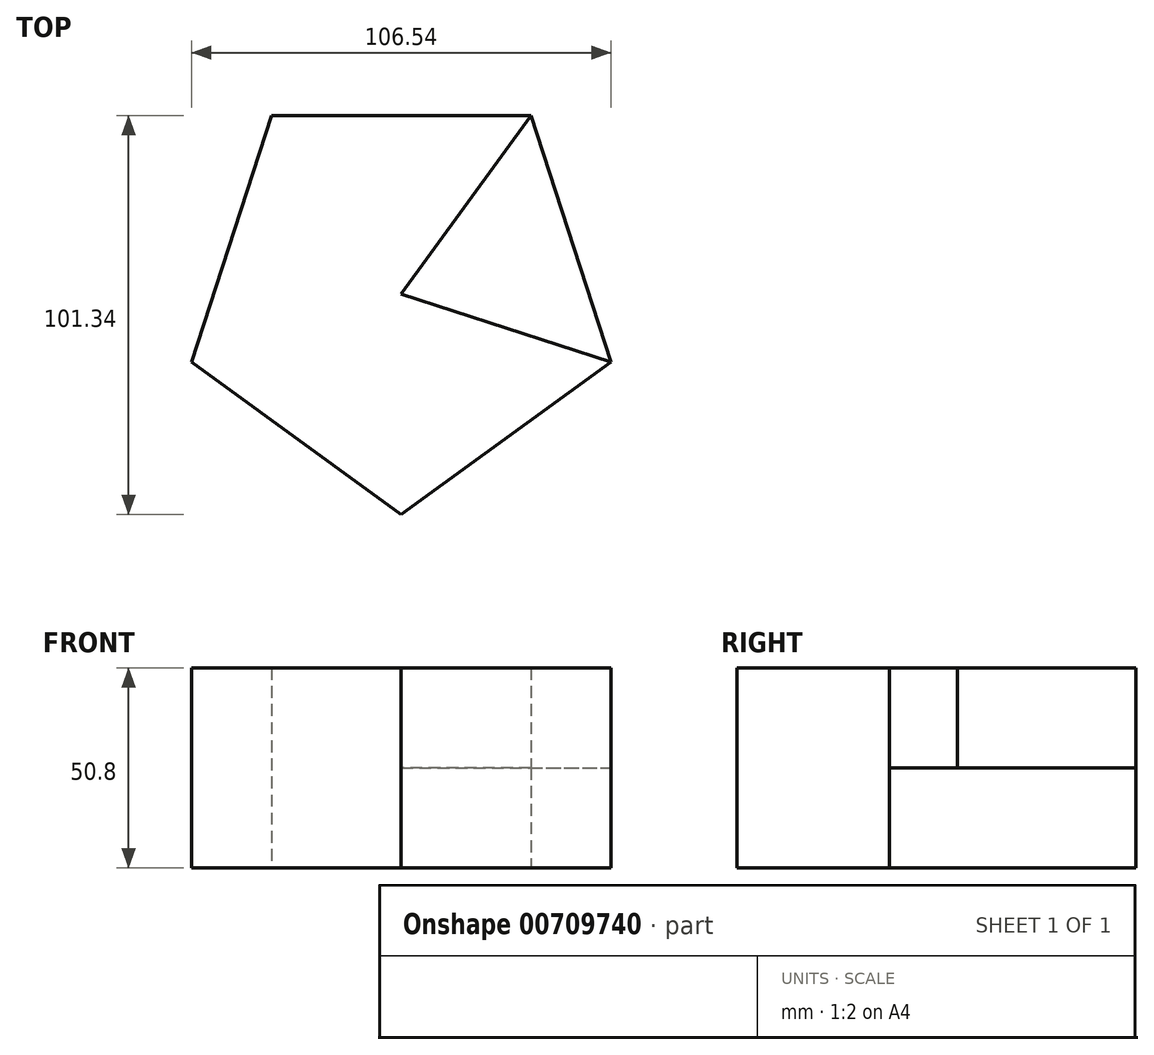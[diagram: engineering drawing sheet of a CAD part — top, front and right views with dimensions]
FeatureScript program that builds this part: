
annotation { "Feature Type Name" : "Feature", "Feature Type Description" : "" }
export const myFeature = defineFeature(function(context is Context, id is Id, definition is map)
    precondition{}
    {
        {
            var Q0;
            Q0=qCreatedBy(makeId("Top.planeOp"),FACE);
            var sketch = newSketch(context, id + "F0", { "sketchPlane" : qUnion([Q0])});
            skCircle(sketch, "E0.cCircle", {"center": v(0, 0) * mm, "radius": 45.32 * mm, "construction": true});
            skLineSegment(sketch, "E0.0", {"start": v(-32.93, 45.32) * mm, "end": v(32.93, 45.32) * mm});
            skLineSegment(sketch, "E0.1", {"start": v(32.93, 45.32) * mm, "end": v(53.27, -17.3) * mm});
            skLineSegment(sketch, "E0.2", {"start": v(53.27, -17.3) * mm, "end": v(0, -56.02) * mm});
            skLineSegment(sketch, "E0.3", {"start": v(0, -56.02) * mm, "end": v(-53.27, -17.3) * mm});
            skLineSegment(sketch, "E0.4", {"start": v(-53.27, -17.3) * mm, "end": v(-32.93, 45.32) * mm});
            skPoint(sketch, "E0.0.midPoint", {"position": v(0, 45.32) * mm});
            skSolve(sketch);
        }
        {
            var Q0;
            Q0=makeQuery(id+"F0.imprint","IMPRINT",FACE,{"disambiguationData":[TD([[makeQuery(id+"F0.imprint","IMPRINT",EDGE,{"derivedFrom":sQuery(id+"F0.wireOp",EDGE,"E0.0")}),-1.0]])]});
            extrude(context, id + "F1", {"entities" : qUnion([Q0]), "depth" : 25.4 * mm, "offsetDistance" : 25.4 * mm});
        }
        {
            var Q0;
            Q0=makeQuery(id+"F1.opExtrude","CAP_FACE",FACE,{"disambiguationData":[OSD([sQuery(id+"F0.wireOp",EDGE,"E0.0"),sQuery(id+"F0.wireOp",EDGE,"E0.1"),sQuery(id+"F0.wireOp",EDGE,"E0.2"),sQuery(id+"F0.wireOp",EDGE,"E0.3"),sQuery(id+"F0.wireOp",EDGE,"E0.4")])],"isStart":false});
            var sketch = newSketch(context, id + "F2", { "sketchPlane" : qUnion([Q0])});
            skLineSegment(sketch, "E1", {"start": v(32.93, 45.32) * mm, "end": v(0, 0) * mm});
            skLineSegment(sketch, "E2", {"start": v(0, 0) * mm, "end": v(53.27, -17.3) * mm});
            skSolve(sketch);
        }
        {
            var Q0;
            Q0=makeQuery(id+"F2.imprint","IMPRINT",FACE,{"disambiguationData":[TD([[makeQuery(id+"F2.imprint","IMPRINT",EDGE,{"derivedFrom":sQuery(id+"F2.wireOp",EDGE,"E1")}),-1.0]])]});
            extrude(context, id + "F3", {"entities" : qUnion([Q0]), "operationType" : NewBodyOperationType.ADD, "depth" : 25.4 * mm, "offsetDistance" : 25.4 * mm});
        }
    });
